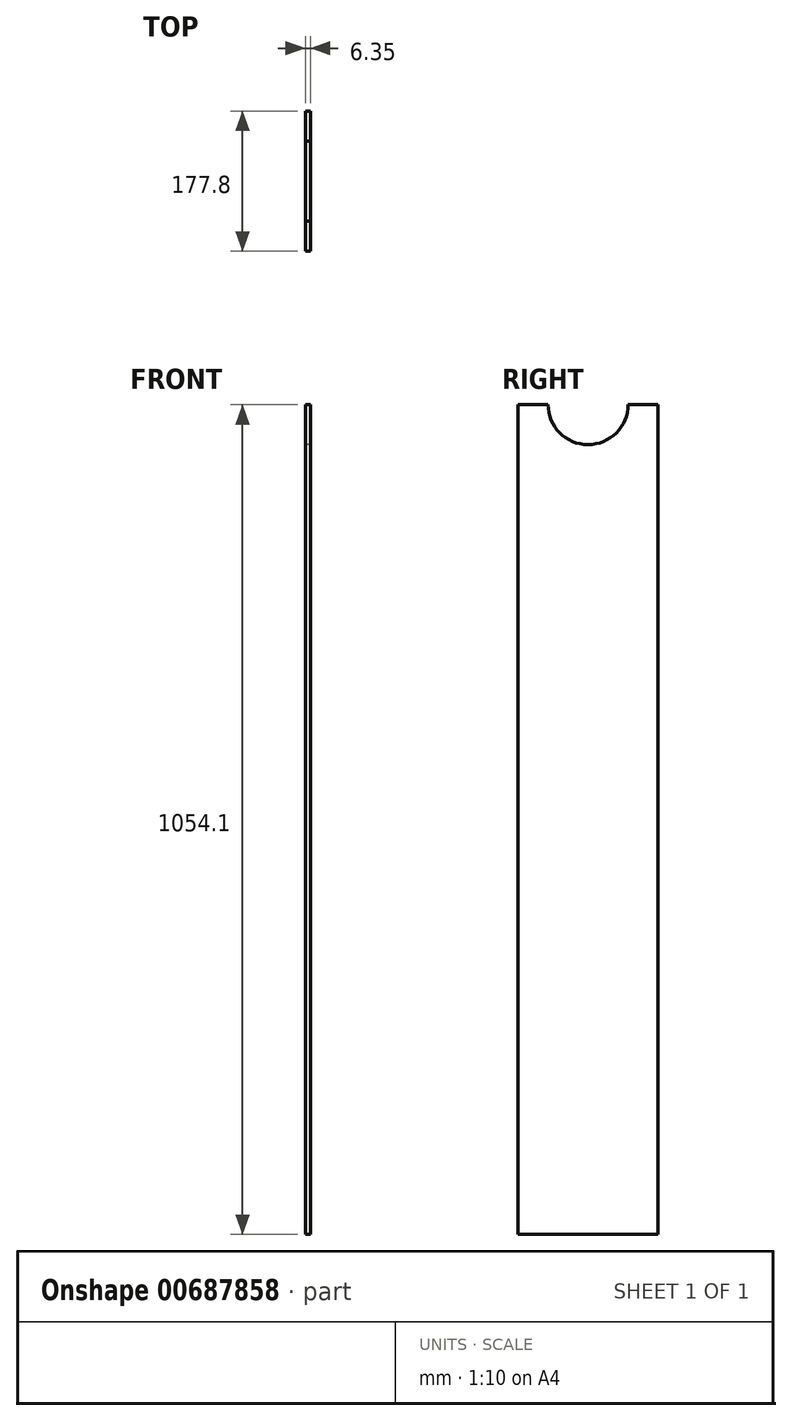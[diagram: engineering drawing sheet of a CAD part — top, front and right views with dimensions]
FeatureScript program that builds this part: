
annotation { "Feature Type Name" : "Feature", "Feature Type Description" : "" }
export const myFeature = defineFeature(function(context is Context, id is Id, definition is map)
    precondition{}
    {
        {
            var Q0;
            Q0=qCreatedBy(makeId("Right.planeOp"),FACE);
            var sketch = newSketch(context, id + "F0", { "sketchPlane" : qUnion([Q0])});
            skLineSegment(sketch, "E0.bottom", {"start": v(88.9, 527.05) * mm, "end": v(-88.9, 527.05) * mm});
            skLineSegment(sketch, "E0.top", {"start": v(88.9, -527.05) * mm, "end": v(-88.9, -527.05) * mm});
            skLineSegment(sketch, "E0.left", {"start": v(88.9, 527.05) * mm, "end": v(88.9, -527.05) * mm});
            skLineSegment(sketch, "E0.right", {"start": v(-88.9, 527.05) * mm, "end": v(-88.9, -527.05) * mm});
            skPoint(sketch, "E0.middle", {"position": v(0, 0) * mm});
            skCircle(sketch, "E1", {"center": v(0, 527.05) * mm, "radius": 50.8 * mm});
            skSolve(sketch);
        }
        {
            var Q0;
            Q0=makeQuery(id+"F0.imprint","IMPRINT",FACE,{"disambiguationData":[TD([[makeQuery(id+"F0.imprint","IMPRINT",EDGE,{"derivedFrom":sQuery(id+"F0.wireOp",EDGE,"E0.top")}),-1.0]])]});
            extrude(context, id + "F1", {"entities" : qUnion([Q0]), "depth" : 6.35 * mm, "offsetDistance" : 25.4 * mm});
        }
    });
